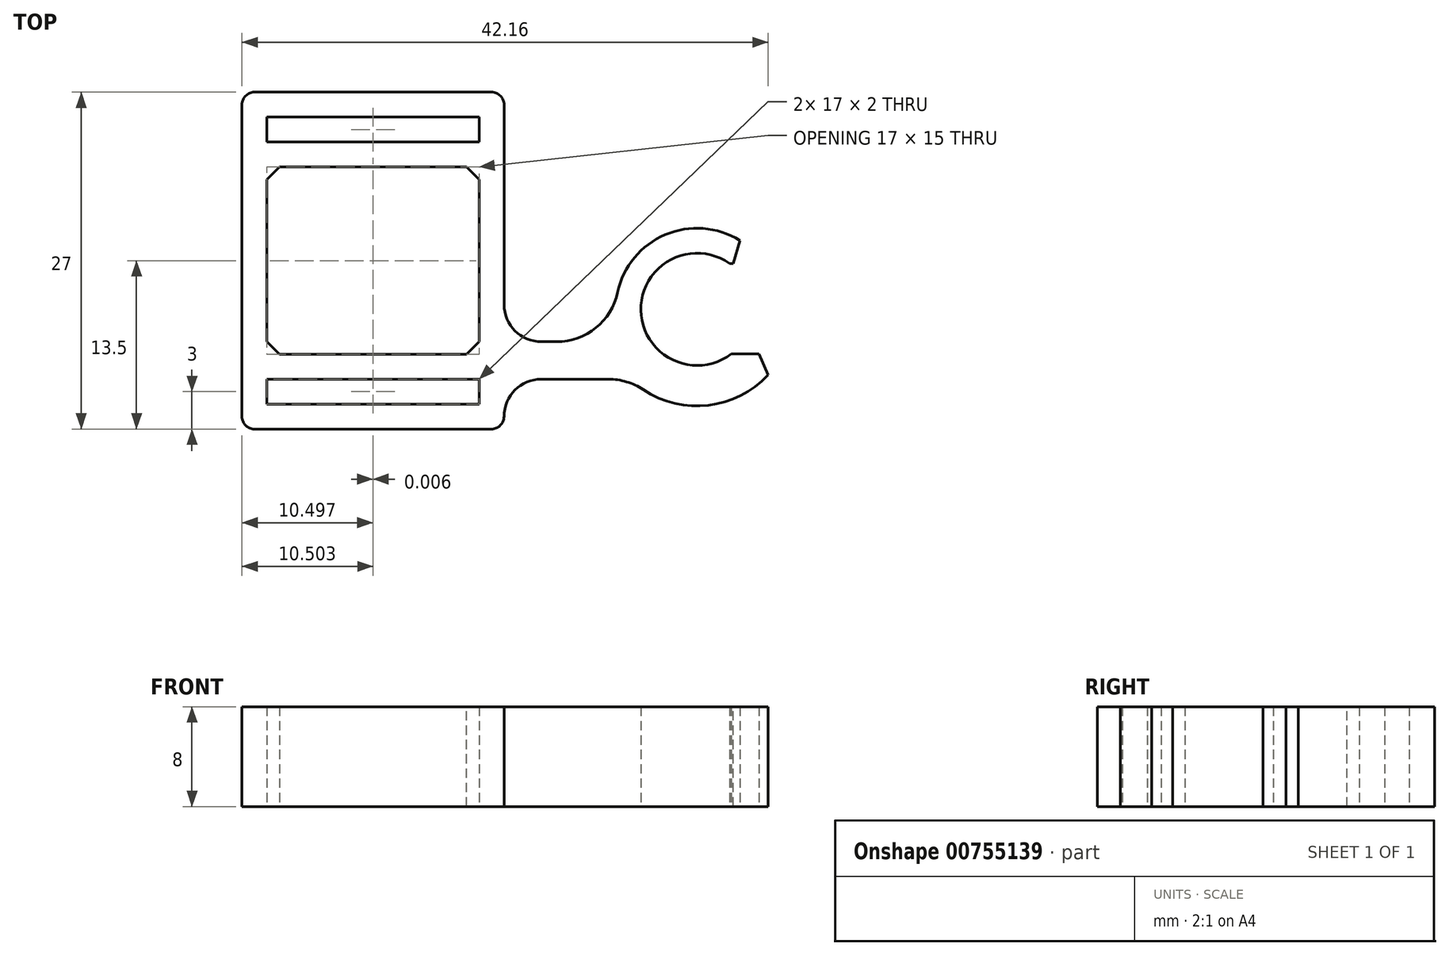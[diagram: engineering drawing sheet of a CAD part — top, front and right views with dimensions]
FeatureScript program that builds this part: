
annotation { "Feature Type Name" : "Feature", "Feature Type Description" : "" }
export const myFeature = defineFeature(function(context is Context, id is Id, definition is map)
    precondition{}
    {
        {
            var Q0;
            Q0=qCreatedBy(makeId("Top.planeOp"),FACE);
            var sketch = newSketch(context, id + "F0", { "sketchPlane" : qUnion([Q0])});
            skArc(sketch, "E0", {"start": v(2.6, 3.67) * mm, "mid": v(-4.5, -0.08) * mm, "end": v(2.73, -3.57) * mm});
            skArc(sketch, "E1", {"start": v(5.36, 3.67) * mm, "mid": v(-3.15, 5.69) * mm, "end": v(-5.96, -2.6) * mm});
            skLineSegment(sketch, "E2", {"start": v(-5.96, -2.6) * mm, "end": v(-15.46, -2.6) * mm});
            skArc(sketch, "E3", {"start": v(-5.36, -5.6) * mm, "mid": v(1.26, -7.65) * mm, "end": v(6.88, -3.57) * mm});
            skLineSegment(sketch, "E4", {"start": v(-34.46, -5.6) * mm, "end": v(-17.46, -5.6) * mm});
            skLineSegment(sketch, "E5", {"start": v(-36.46, -9.6) * mm, "end": v(-15.46, -9.6) * mm});
            skLineSegment(sketch, "E6", {"start": v(-34.46, -7.6) * mm, "end": v(-17.46, -7.6) * mm});
            skLineSegment(sketch, "E7", {"start": v(-34.46, -5.6) * mm, "end": v(-34.46, -7.6) * mm});
            skLineSegment(sketch, "E8", {"start": v(-17.46, -5.6) * mm, "end": v(-17.46, -7.6) * mm});
            skLineSegment(sketch, "E9", {"start": v(-34.46, 11.4) * mm, "end": v(-34.46, -3.6) * mm});
            skLineSegment(sketch, "E10", {"start": v(-34.46, -3.6) * mm, "end": v(-17.46, -3.6) * mm});
            skLineSegment(sketch, "E11", {"start": v(-17.46, 11.4) * mm, "end": v(-17.46, -3.6) * mm});
            skLineSegment(sketch, "E12", {"start": v(-15.46, -5.6) * mm, "end": v(-15.46, -9.6) * mm});
            skLineSegment(sketch, "E13", {"start": v(-15.46, -5.6) * mm, "end": v(-5.36, -5.6) * mm});
            skLineSegment(sketch, "E14", {"start": v(-34.46, 11.4) * mm, "end": v(-17.46, 11.4) * mm});
            skLineSegment(sketch, "E15", {"start": v(-36.46, -9.6) * mm, "end": v(-36.46, 11.4) * mm});
            skLineSegment(sketch, "E16", {"start": v(-15.46, 13.4) * mm, "end": v(-15.46, -2.6) * mm});
            skLineSegment(sketch, "E17", {"start": v(-36.46, 11.4) * mm, "end": v(-36.46, 17.4) * mm});
            skLineSegment(sketch, "E18", {"start": v(-36.46, 17.4) * mm, "end": v(-15.46, 17.4) * mm});
            skLineSegment(sketch, "E19", {"start": v(-15.46, 17.4) * mm, "end": v(-15.46, 13.4) * mm});
            skLineSegment(sketch, "E20", {"start": v(-34.46, 13.4) * mm, "end": v(-34.46, 15.4) * mm});
            skLineSegment(sketch, "E21", {"start": v(-34.46, 15.4) * mm, "end": v(-17.46, 15.4) * mm});
            skLineSegment(sketch, "E22", {"start": v(-17.46, 15.4) * mm, "end": v(-17.46, 13.4) * mm});
            skLineSegment(sketch, "E23", {"start": v(-17.46, 13.4) * mm, "end": v(-34.46, 13.4) * mm});
            skLineSegment(sketch, "E24", {"start": v(2.73, -3.57) * mm, "end": v(6.88, -3.57) * mm});
            skLineSegment(sketch, "E25", {"start": v(2.6, 3.67) * mm, "end": v(5.36, 3.67) * mm});
            skSolve(sketch);
        }
        {
            var Q0;
            Q0=qSketchRegion(id+"F0",true);
            extrude(context, id + "F1", {"entities" : qUnion([Q0]), "depth" : 8 * mm, "offsetDistance" : 25 * mm});
        }
        {
            var Q0;
            Q0=makeQuery(id+"F1.opExtrude","SWEPT_EDGE",EDGE,{"disambiguationData":[OSD([sQuery(id+"F0.wireOp",EDGE,"E1"),sQuery(id+"F0.wireOp",EDGE,"E2")])]});
            var Q1;
            Q1=makeQuery(id+"F1.opExtrude","SWEPT_EDGE",EDGE,{"disambiguationData":[OSD([sQuery(id+"F0.wireOp",EDGE,"E3"),sQuery(id+"F0.wireOp",EDGE,"E13")])]});
            fillet(context, id + "F2", {"entities" : qUnion([Q0, Q1]), "radius" : 5 * mm, "tangentPropagation" : true, "allowEdgeOverflow" : false});
        }
        {
            var Q0;
            Q0=makeQuery(id+"F1.opExtrude","SWEPT_EDGE",EDGE,{"disambiguationData":[OSD([sQuery(id+"F0.wireOp",EDGE,"qlEsCMng-nP1c-Ekt7-Tyx7-aruzIJqyAlro"),sQuery(id+"F0.wireOp",EDGE,"E9")])]});
            var Q1;
            Q1=makeQuery(id+"F1.opExtrude","SWEPT_EDGE",EDGE,{"disambiguationData":[OSD([sQuery(id+"F0.wireOp",EDGE,"7MTTxkCb-1jcS-6ybF-nzqN-XLByJkMF9NAO"),sQuery(id+"F0.wireOp",EDGE,"E11")])]});
            var Q2;
            Q2=makeQuery(id+"F1.opExtrude","SWEPT_EDGE",EDGE,{"disambiguationData":[OSD([sQuery(id+"F0.wireOp",EDGE,"E1"),sQuery(id+"F0.wireOp",EDGE,"xk6Xs0EH-QGaJ-X7Y0-ESvd-E0XzonEpn0qV")])]});
            var Q3;
            Q3=makeQuery(id+"F1.opExtrude","SWEPT_EDGE",EDGE,{"disambiguationData":[OSD([sQuery(id+"F0.wireOp",EDGE,"E3"),sQuery(id+"F0.wireOp",EDGE,"vBpwUBgh-lr2c-6uub-pIzf-sdJIbTrYbDT1")])]});
            chamfer(context, id + "F3", {"entities" : qUnion([Q0, Q1, Q2, Q3]), "width" : 1 * mm, "tangentPropagation" : true});
        }
        {
            var Q0;
            Q0=makeQuery(id+"F1.opExtrude","SWEPT_EDGE",EDGE,{"disambiguationData":[OSD([sQuery(id+"F0.wireOp",EDGE,"E5"),sQuery(id+"F0.wireOp",EDGE,"pjbQi6Rr-9b1S-VNNr-jyuV-W8fq62JQzEaZ")])]});
            var Q1;
            Q1=makeQuery(id+"F1.opExtrude","SWEPT_EDGE",EDGE,{"disambiguationData":[OSD([sQuery(id+"F0.wireOp",EDGE,"E5"),sQuery(id+"F0.wireOp",EDGE,"E12")])]});
            var Q2;
            Q2=makeQuery(id+"F1.opExtrude","SWEPT_EDGE",EDGE,{"disambiguationData":[OSD([sQuery(id+"F0.wireOp",EDGE,"E17"),sQuery(id+"F0.wireOp",EDGE,"E18")])]});
            var Q3;
            Q3=makeQuery(id+"F1.opExtrude","SWEPT_EDGE",EDGE,{"disambiguationData":[OSD([sQuery(id+"F0.wireOp",EDGE,"E18"),sQuery(id+"F0.wireOp",EDGE,"E19")])]});
            fillet(context, id + "F4", {"entities" : qUnion([Q0, Q1, Q2, Q3]), "radius" : 1 * mm, "tangentPropagation" : true, "allowEdgeOverflow" : false});
        }
        {
            var Q0;
            Q0=makeQuery(id+"F1.opExtrude","SWEPT_EDGE",EDGE,{"disambiguationData":[OSD([sQuery(id+"F0.wireOp",EDGE,"E2"),sQuery(id+"F0.wireOp",EDGE,"E16")])]});
            var Q1;
            Q1=makeQuery(id+"F1.opExtrude","SWEPT_EDGE",EDGE,{"disambiguationData":[OSD([sQuery(id+"F0.wireOp",EDGE,"E12"),sQuery(id+"F0.wireOp",EDGE,"E13")])]});
            fillet(context, id + "F5", {"entities" : qUnion([Q0, Q1]), "radius" : 3 * mm, "tangentPropagation" : true, "allowEdgeOverflow" : false});
        }
    });
